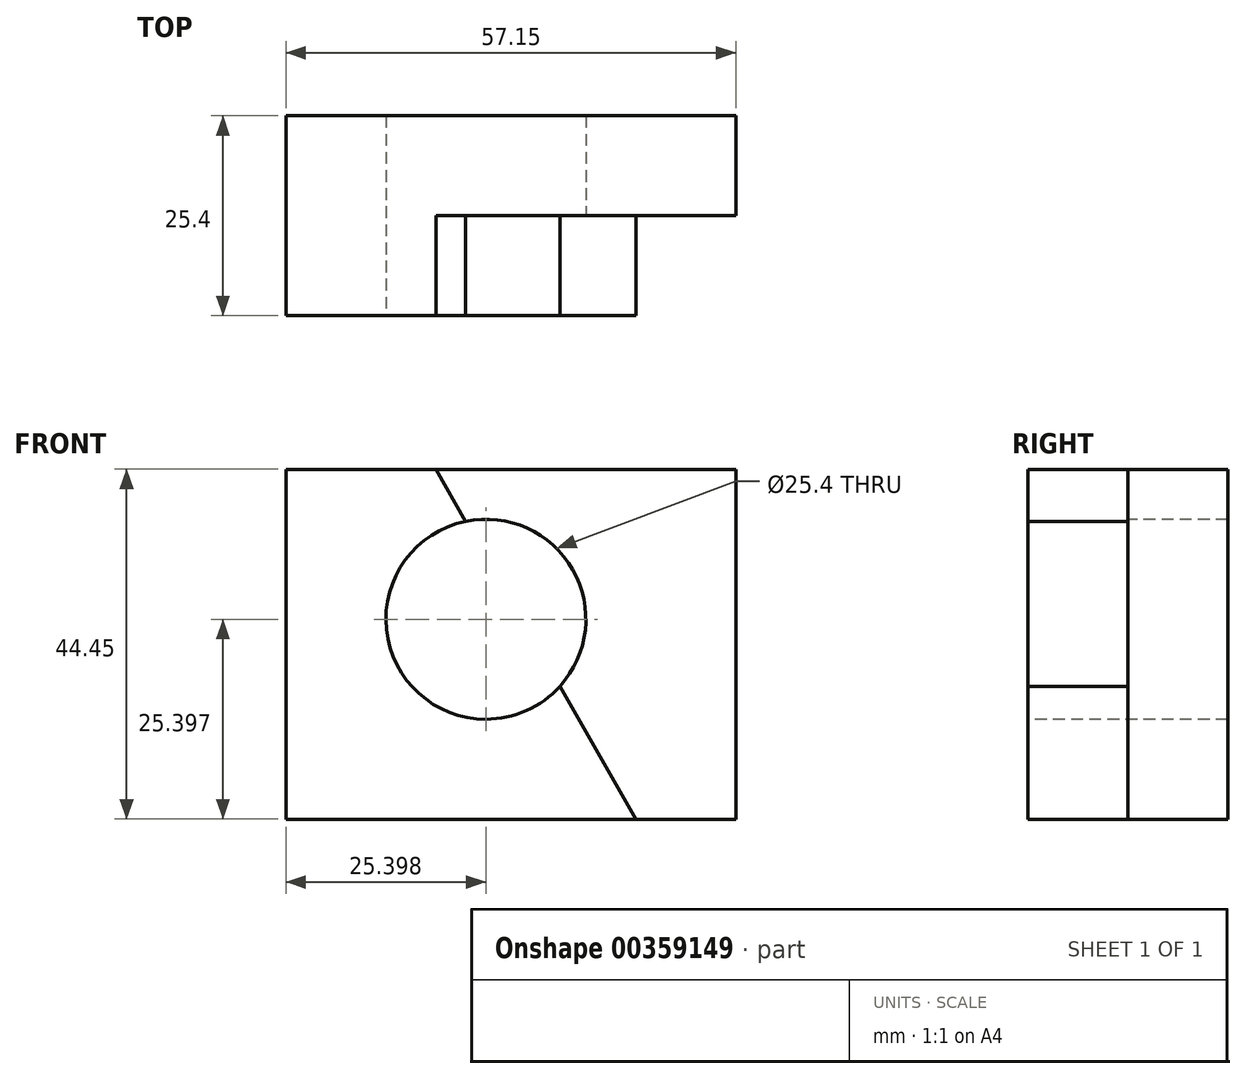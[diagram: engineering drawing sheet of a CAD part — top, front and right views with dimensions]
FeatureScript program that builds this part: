
annotation { "Feature Type Name" : "Feature", "Feature Type Description" : "" }
export const myFeature = defineFeature(function(context is Context, id is Id, definition is map)
    precondition{}
    {
        {
            var Q0;
            Q0=qCreatedBy(makeId("Front.planeOp"),FACE);
            var sketch = newSketch(context, id + "F0", { "sketchPlane" : qUnion([Q0])});
            skLineSegment(sketch, "E0.bottom", {"start": v(-18.22, 28.24) * mm, "end": v(38.93, 28.24) * mm});
            skLineSegment(sketch, "E0.top", {"start": v(-18.22, -16.21) * mm, "end": v(38.93, -16.21) * mm});
            skLineSegment(sketch, "E0.left", {"start": v(-18.22, 28.24) * mm, "end": v(-18.22, -16.21) * mm});
            skLineSegment(sketch, "E0.right", {"start": v(38.93, 28.24) * mm, "end": v(38.93, -16.21) * mm});
            skSolve(sketch);
        }
        {
            var Q0;
            Q0 = qSketchRegion(id + "F0", true);
            extrude(context, id + "F1", {"entities" : qUnion([Q0]), "depth" : 25.4 * mm});
        }
        {
            var Q0;
            Q0=makeQuery(id+"F1.opExtrude","CAP_FACE",FACE,{"disambiguationData":[OSD([sQuery(id+"F0.wireOp",EDGE,"E0.bottom"),sQuery(id+"F0.wireOp",EDGE,"E0.top"),sQuery(id+"F0.wireOp",EDGE,"E0.left"),sQuery(id+"F0.wireOp",EDGE,"E0.right")])],"isStart":false});
            var sketch = newSketch(context, id + "F2", { "sketchPlane" : qUnion([Q0])});
            skLineSegment(sketch, "E1", {"start": v(0.83, 28.24) * mm, "end": v(26.23, -16.21) * mm});
            skCircle(sketch, "E2", {"center": v(7.18, 9.19) * mm, "radius": 12.7 * mm});
            skSolve(sketch);
        }
        {
            var Q0;
            {var subQ0=sQuery(id+"F2.wireOp",EDGE,"E2");var subQ1=sQuery(id+"F2.wireOp",EDGE,"E1");var subQ2=makeQuery(id+"F2.imprint","INTERSECT",VERTEX,{"disambiguationData":[OD(0.0)],"derivedFrom":[subQ1,subQ0]});Q0=makeQuery(id+"F2.imprint","IMPRINT",FACE,{"disambiguationData":[TD([[makeQuery(id+"F2.imprint","IMPRINT",EDGE,{"disambiguationData":[TD([[subQ2,-1.0]])],"derivedFrom":subQ1}),-1.0]])]});}
            var Q1;
            {var subQ0=sQuery(id+"F2.wireOp",EDGE,"E2");var subQ1=sQuery(id+"F2.wireOp",EDGE,"E1");var subQ2=makeQuery(id+"F2.imprint","INTERSECT",VERTEX,{"disambiguationData":[OD(0.0)],"derivedFrom":[subQ1,subQ0]});Q1=makeQuery(id+"F2.imprint","IMPRINT",FACE,{"disambiguationData":[TD([[makeQuery(id+"F2.imprint","IMPRINT",EDGE,{"disambiguationData":[TD([[subQ2,-1.0]])],"derivedFrom":subQ1}),1.0]])]});}
            extrude(context, id + "F3", {"entities" : qUnion([Q0, Q1]), "operationType" : NewBodyOperationType.REMOVE, "oppositeDirection" : true, "depth" : 25.4 * mm});
        }
        {
            var Q0;
            {var subQ0=makeQuery(id+"F1.opExtrude","CAP_EDGE",EDGE,{"disambiguationData":[OSD([sQuery(id+"F0.wireOp",EDGE,"E0.right")])],"isStart":false});Q0=makeQuery(id+"F2.imprint","IMPRINT",FACE,{"disambiguationData":[TD([[makeQuery(id+"F2.imprint","IMPRINT",EDGE,{"derivedFrom":subQ0}),-1.0]])]});}
            var Q1;
            {var subQ0=sQuery(id+"F2.wireOp",EDGE,"E2");var subQ1=sQuery(id+"F2.wireOp",EDGE,"E1");var subQ2=makeQuery(id+"F2.imprint","INTERSECT",VERTEX,{"disambiguationData":[OD(0.0)],"derivedFrom":[subQ1,subQ0]});Q1=makeQuery(id+"F2.imprint","IMPRINT",FACE,{"disambiguationData":[TD([[makeQuery(id+"F2.imprint","IMPRINT",EDGE,{"disambiguationData":[TD([[subQ2,-1.0]])],"derivedFrom":subQ1}),1.0]])]});}
            var Q2;
            {var subQ0=sQuery(id+"F2.wireOp",EDGE,"E2");var subQ1=sQuery(id+"F2.wireOp",EDGE,"E1");var subQ2=makeQuery(id+"F2.imprint","INTERSECT",VERTEX,{"disambiguationData":[OD(0.0)],"derivedFrom":[subQ1,subQ0]});Q2=makeQuery(id+"F2.imprint","IMPRINT",FACE,{"disambiguationData":[TD([[makeQuery(id+"F2.imprint","IMPRINT",EDGE,{"disambiguationData":[TD([[subQ2,-1.0]])],"derivedFrom":subQ1}),-1.0]])]});}
            extrude(context, id + "F4", {"entities" : qUnion([Q0, Q1, Q2]), "operationType" : NewBodyOperationType.REMOVE, "oppositeDirection" : true, "depth" : 12.7 * mm});
        }
    });
